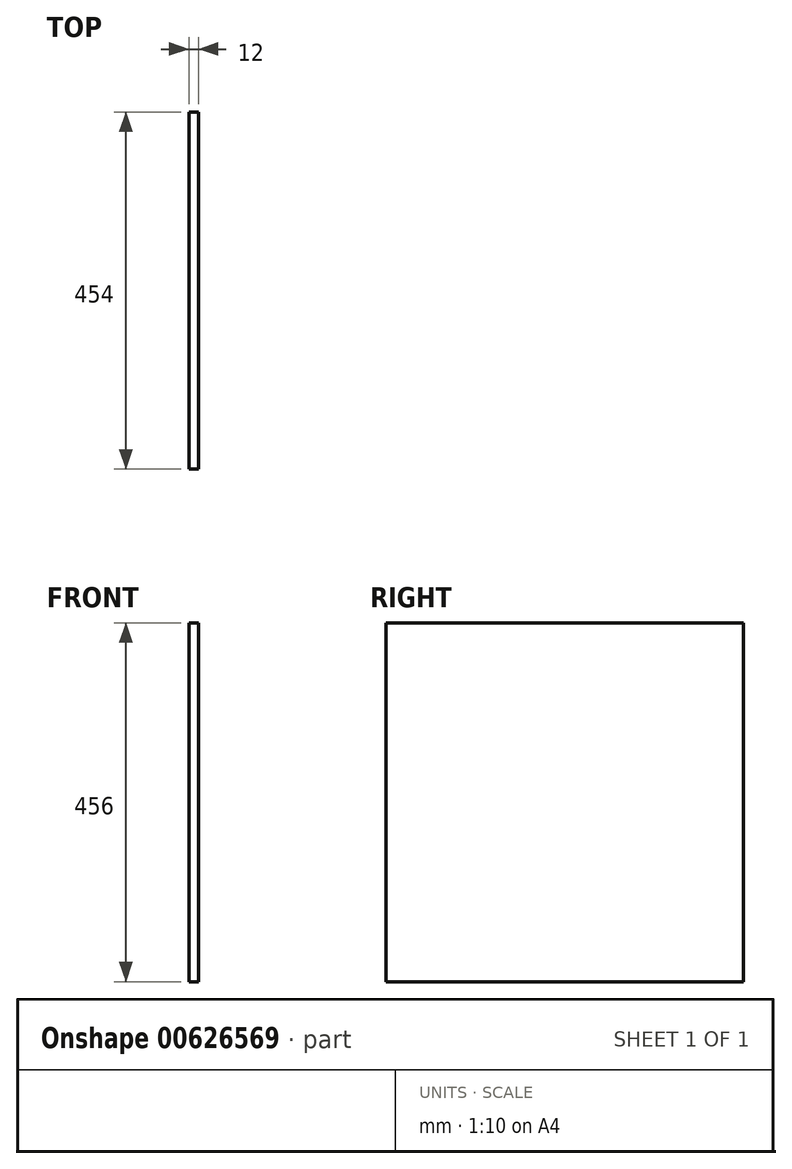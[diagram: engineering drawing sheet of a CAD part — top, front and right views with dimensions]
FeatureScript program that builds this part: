
annotation { "Feature Type Name" : "Feature", "Feature Type Description" : "" }
export const myFeature = defineFeature(function(context is Context, id is Id, definition is map)
    precondition{}
    {
        {
            assignVariable(context, id + "F0", {"name" : "thickness", "anyValue" : 12});
        }
        {
            var Q0;
            Q0=qCreatedBy(makeId("Right.planeOp"),FACE);
            var sketch = newSketch(context, id + "F1", { "sketchPlane" : qUnion([Q0])});
            skLineSegment(sketch, "E0.bottom", {"start": v(-227, 228) * mm, "end": v(227, 228) * mm});
            skLineSegment(sketch, "E0.top", {"start": v(-227, -228) * mm, "end": v(227, -228) * mm});
            skLineSegment(sketch, "E0.left", {"start": v(-227, 228) * mm, "end": v(-227, -228) * mm});
            skLineSegment(sketch, "E0.right", {"start": v(227, 228) * mm, "end": v(227, -228) * mm});
            skPoint(sketch, "E0.middle", {"position": v(0, 0) * mm});
            skSolve(sketch);
        }
        {
            var Q0;
            Q0=makeQuery(id+"F1.imprint","IMPRINT",FACE,{"disambiguationData":[TD([[makeQuery(id+"F1.imprint","IMPRINT",EDGE,{"derivedFrom":sQuery(id+"F1.wireOp",EDGE,"E0.bottom")}),-1.0]])]});
            extrude(context, id + "F2", {"entities" : qUnion([Q0]), "depth" : (getVariable(context, 'thickness')) * mm});
        }
    });
